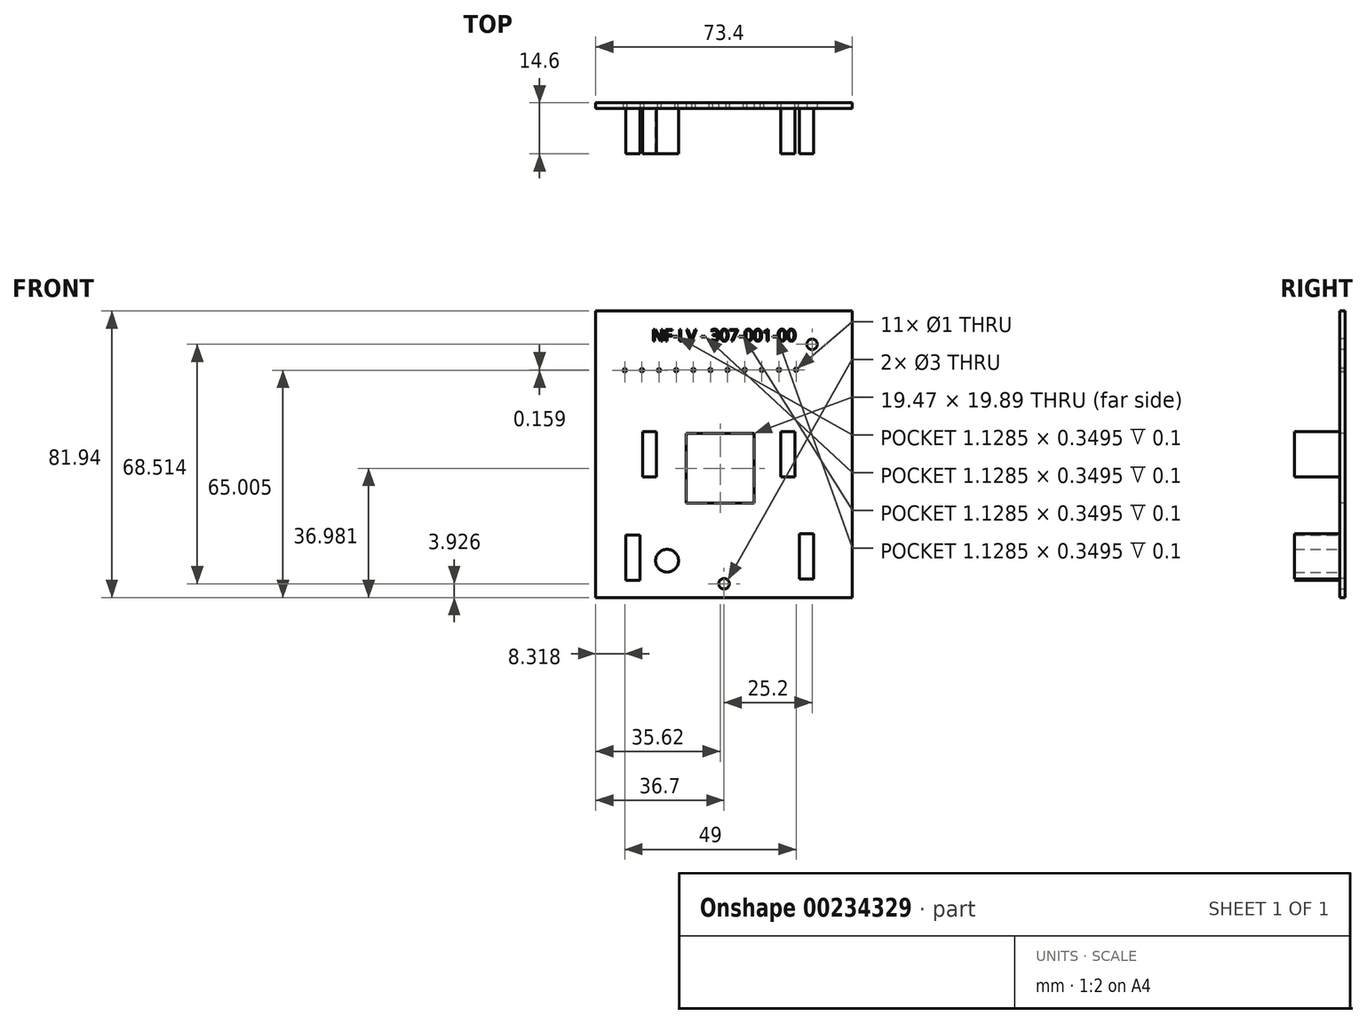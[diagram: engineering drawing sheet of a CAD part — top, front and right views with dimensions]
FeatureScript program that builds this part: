
annotation { "Feature Type Name" : "Feature", "Feature Type Description" : "" }
export const myFeature = defineFeature(function(context is Context, id is Id, definition is map)
    precondition{}
    {
        {
            var Q0;
            Q0=qCreatedBy(makeId("Front.planeOp"),FACE);
            var sketch = newSketch(context, id + "F0", { "sketchPlane" : qUnion([Q0])});
            skLineSegment(sketch, "E0.bottom", {"start": v(36.7, -40.97) * mm, "end": v(-36.7, -40.97) * mm});
            skLineSegment(sketch, "E0.top", {"start": v(36.7, 40.97) * mm, "end": v(-36.7, 40.97) * mm});
            skLineSegment(sketch, "E0.left", {"start": v(36.7, -40.97) * mm, "end": v(36.7, 40.97) * mm});
            skLineSegment(sketch, "E0.right", {"start": v(-36.7, -40.97) * mm, "end": v(-36.7, 40.97) * mm});
            skPoint(sketch, "E0.middle", {"position": v(0, 0) * mm});
            skLineSegment(sketch, "E1.bottom", {"start": v(8.65, -13.93) * mm, "end": v(-10.81, -13.93) * mm});
            skLineSegment(sketch, "E1.top", {"start": v(8.65, 5.95) * mm, "end": v(-10.81, 5.95) * mm});
            skLineSegment(sketch, "E1.left", {"start": v(8.65, -13.93) * mm, "end": v(8.65, 5.95) * mm});
            skLineSegment(sketch, "E1.right", {"start": v(-10.81, -13.93) * mm, "end": v(-10.81, 5.95) * mm});
            skPoint(sketch, "E1.middle", {"position": v(0, -3) * mm});
            skCircle(sketch, "E2", {"center": v(0, -37.04) * mm, "radius": 1.5 * mm});
            skCircle(sketch, "E3.MirrorC", {"center": v(25.2, 31.47) * mm, "radius": 1.5 * mm});
            skCircle(sketch, "E4", {"center": v(-16.3, -30.45) * mm, "radius": 3.27 * mm});
            skLineSegment(sketch, "E5.bottom", {"start": v(-19.33, -6.5) * mm, "end": v(-23.33, -6.5) * mm});
            skLineSegment(sketch, "E5.top", {"start": v(-19.33, 6.5) * mm, "end": v(-23.33, 6.5) * mm});
            skLineSegment(sketch, "E5.left", {"start": v(-19.33, -6.5) * mm, "end": v(-19.33, 6.5) * mm});
            skLineSegment(sketch, "E5.right", {"start": v(-23.33, -6.5) * mm, "end": v(-23.33, 6.5) * mm});
            skPoint(sketch, "E5.middle", {"position": v(-21.33, 0) * mm});
            skLineSegment(sketch, "E6.bottom", {"start": v(20.25, -6.5) * mm, "end": v(16.25, -6.5) * mm});
            skLineSegment(sketch, "E6.top", {"start": v(20.25, 6.5) * mm, "end": v(16.25, 6.5) * mm});
            skLineSegment(sketch, "E6.left", {"start": v(20.25, -6.5) * mm, "end": v(20.25, 6.5) * mm});
            skLineSegment(sketch, "E6.right", {"start": v(16.25, -6.5) * mm, "end": v(16.25, 6.5) * mm});
            skPoint(sketch, "E6.middle", {"position": v(18.25, 0) * mm});
            skLineSegment(sketch, "E7.bottom", {"start": v(25.6, -35.7) * mm, "end": v(21.6, -35.7) * mm});
            skLineSegment(sketch, "E7.top", {"start": v(25.6, -22.7) * mm, "end": v(21.6, -22.7) * mm});
            skLineSegment(sketch, "E7.left", {"start": v(25.6, -35.7) * mm, "end": v(25.6, -22.7) * mm});
            skLineSegment(sketch, "E7.right", {"start": v(21.6, -35.7) * mm, "end": v(21.6, -22.7) * mm});
            skPoint(sketch, "E7.middle", {"position": v(23.6, -29.2) * mm});
            skLineSegment(sketch, "E8.bottom", {"start": v(-24.06, -36.08) * mm, "end": v(-28.06, -36.08) * mm});
            skLineSegment(sketch, "E8.top", {"start": v(-24.06, -23.08) * mm, "end": v(-28.06, -23.08) * mm});
            skLineSegment(sketch, "E8.left", {"start": v(-24.06, -36.08) * mm, "end": v(-24.06, -23.08) * mm});
            skLineSegment(sketch, "E8.right", {"start": v(-28.06, -36.08) * mm, "end": v(-28.06, -23.08) * mm});
            skPoint(sketch, "E8.middle", {"position": v(-26.06, -29.58) * mm});
            skCircle(sketch, "E9", {"center": v(-28.38, 24.04) * mm, "radius": 0.5 * mm});
            skCircle(sketch, "E10.1.0.0", {"center": v(-23.48, 24.05) * mm, "radius": 0.5 * mm});
            skCircle(sketch, "E10.2.0.0", {"center": v(-18.58, 24.07) * mm, "radius": 0.5 * mm});
            skCircle(sketch, "E10.3.0.0", {"center": v(-13.68, 24.08) * mm, "radius": 0.5 * mm});
            skCircle(sketch, "E10.4.0.0", {"center": v(-8.78, 24.1) * mm, "radius": 0.5 * mm});
            skCircle(sketch, "E10.5.0.0", {"center": v(-3.88, 24.11) * mm, "radius": 0.5 * mm});
            skCircle(sketch, "E10.6.0.0", {"center": v(1.02, 24.13) * mm, "radius": 0.5 * mm});
            skCircle(sketch, "E10.7.0.0", {"center": v(5.92, 24.15) * mm, "radius": 0.5 * mm});
            skCircle(sketch, "E10.8.0.0", {"center": v(10.82, 24.16) * mm, "radius": 0.5 * mm});
            skCircle(sketch, "E10.9.0.0", {"center": v(15.72, 24.18) * mm, "radius": 0.5 * mm});
            skCircle(sketch, "E10.10.0.0", {"center": v(20.62, 24.2) * mm, "radius": 0.5 * mm});
            skLineSegment(sketch, "E10.direction1", {"start": v(-28.38, 24.04) * mm, "end": v(-23.48, 24.05) * mm, "construction": true});
            skSolve(sketch);
        }
        {
            var Q0;
            Q0=makeQuery(id+"F0.imprint","IMPRINT",FACE,{"disambiguationData":[TD([[makeQuery(id+"F0.imprint","IMPRINT",EDGE,{"derivedFrom":sQuery(id+"F0.wireOp",EDGE,"E0.bottom")}),-1.0]])]});
            var Q1;
            Q1=makeQuery(id+"F0.imprint","IMPRINT",FACE,{"disambiguationData":[TD([[makeQuery(id+"F0.imprint","IMPRINT",EDGE,{"derivedFrom":sQuery(id+"F0.wireOp",EDGE,"E5.bottom")}),-1.0]])]});
            var Q2;
            Q2=makeQuery(id+"F0.imprint","IMPRINT",FACE,{"disambiguationData":[TD([[makeQuery(id+"F0.imprint","IMPRINT",EDGE,{"derivedFrom":sQuery(id+"F0.wireOp",EDGE,"E6.bottom")}),-1.0]])]});
            var Q3;
            Q3=makeQuery(id+"F0.imprint","IMPRINT",FACE,{"disambiguationData":[TD([[makeQuery(id+"F0.imprint","IMPRINT",EDGE,{"derivedFrom":sQuery(id+"F0.wireOp",EDGE,"E7.bottom")}),-1.0]])]});
            var Q4;
            Q4=makeQuery(id+"F0.imprint","IMPRINT",FACE,{"disambiguationData":[TD([[makeQuery(id+"F0.imprint","IMPRINT",EDGE,{"derivedFrom":sQuery(id+"F0.wireOp",EDGE,"E4")}),1.0]])]});
            var Q5;
            Q5=makeQuery(id+"F0.imprint","IMPRINT",FACE,{"disambiguationData":[TD([[makeQuery(id+"F0.imprint","IMPRINT",EDGE,{"derivedFrom":sQuery(id+"F0.wireOp",EDGE,"E8.bottom")}),-1.0]])]});
            extrude(context, id + "F1", {"entities" : qUnion([Q0, Q1, Q2, Q3, Q4, Q5]), "oppositeDirection" : true, "depth" : 1.6 * mm, "offsetDistance" : 25 * mm});
        }
        {
            var Q0;
            Q0=makeQuery(id+"F1.opExtrude","CAP_FACE",FACE,{"disambiguationData":[OSD([sQuery(id+"F0.wireOp",EDGE,"E0.bottom"),sQuery(id+"F0.wireOp",EDGE,"E0.top"),sQuery(id+"F0.wireOp",EDGE,"E0.left"),sQuery(id+"F0.wireOp",EDGE,"E0.right"),sQuery(id+"F0.wireOp",EDGE,"E1.bottom"),sQuery(id+"F0.wireOp",EDGE,"E1.top"),sQuery(id+"F0.wireOp",EDGE,"E1.left"),sQuery(id+"F0.wireOp",EDGE,"E1.right"),sQuery(id+"F0.wireOp",EDGE,"Hgm9NVbQ-eeb8-uhvC-JqKY-jG901DUjHW5Q"),sQuery(id+"F0.wireOp",EDGE,"E2"),sQuery(id+"F0.wireOp",EDGE,"E3.MirrorC")])],"isStart":true});
            var sketch = newSketch(context, id + "F2", { "sketchPlane" : qUnion([Q0])});
            skText(sketch, "E11", { "text": "NF-LV - 307-001-00", "fontName": "OpenSans-Regular.ttf"});
            const initialGuessF2  = {"E11": [-0.02065, 0.03239, 1, 0, 0.00339]};
            skSetInitialGuess(sketch, initialGuessF2);
            skSolve(sketch);
        }
        {
            var Q0;
            Q0 = qSketchRegion(id + "F2", true);
            extrude(context, id + "F3", {"entities" : qUnion([Q0]), "operationType" : NewBodyOperationType.REMOVE, "oppositeDirection" : true, "depth" : .1 * mm});
        }
        {
            var Q0;
            Q0=makeQuery(id+"F0.imprint","IMPRINT",FACE,{"disambiguationData":[TD([[makeQuery(id+"F0.imprint","IMPRINT",EDGE,{"derivedFrom":sQuery(id+"F0.wireOp",EDGE,"E5.bottom")}),-1.0]])]});
            var Q1;
            Q1=makeQuery(id+"F0.imprint","IMPRINT",FACE,{"disambiguationData":[TD([[makeQuery(id+"F0.imprint","IMPRINT",EDGE,{"derivedFrom":sQuery(id+"F0.wireOp",EDGE,"E6.bottom")}),-1.0]])]});
            var Q2;
            Q2=makeQuery(id+"F0.imprint","IMPRINT",FACE,{"disambiguationData":[TD([[makeQuery(id+"F0.imprint","IMPRINT",EDGE,{"derivedFrom":sQuery(id+"F0.wireOp",EDGE,"E4")}),1.0]])]});
            var Q3;
            Q3=makeQuery(id+"F0.imprint","IMPRINT",FACE,{"disambiguationData":[TD([[makeQuery(id+"F0.imprint","IMPRINT",EDGE,{"derivedFrom":sQuery(id+"F0.wireOp",EDGE,"E8.bottom")}),-1.0]])]});
            var Q4;
            Q4=makeQuery(id+"F0.imprint","IMPRINT",FACE,{"disambiguationData":[TD([[makeQuery(id+"F0.imprint","IMPRINT",EDGE,{"derivedFrom":sQuery(id+"F0.wireOp",EDGE,"E7.bottom")}),-1.0]])]});
            extrude(context, id + "F4", {"entities" : qUnion([Q0, Q1, Q2, Q3, Q4]), "operationType" : NewBodyOperationType.ADD, "depth" : 13 * mm, "offsetDistance" : 25 * mm});
        }
    });
